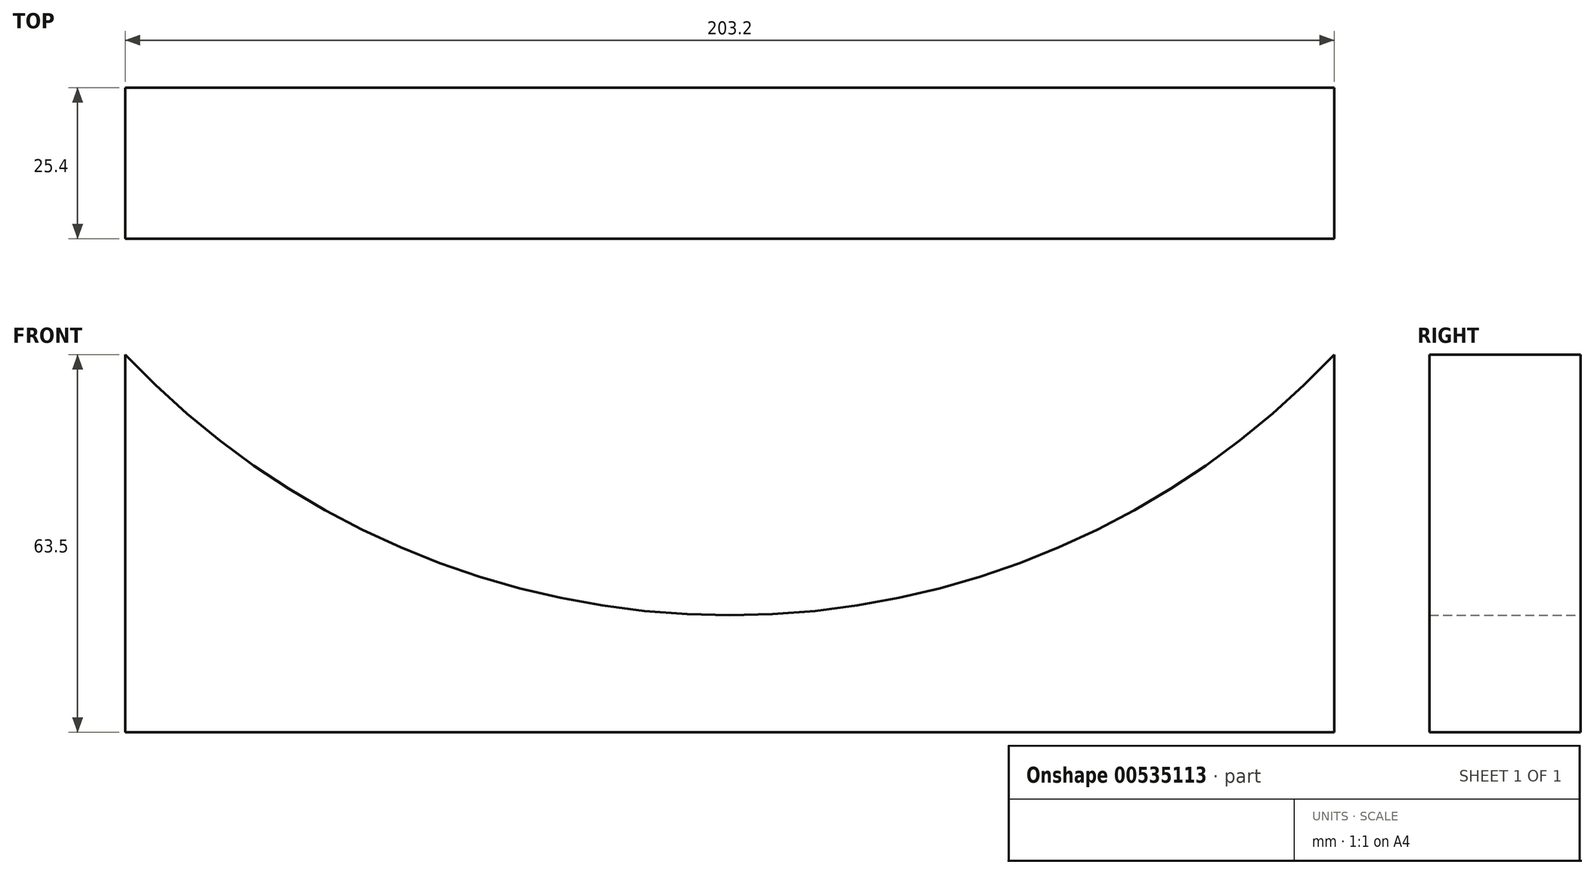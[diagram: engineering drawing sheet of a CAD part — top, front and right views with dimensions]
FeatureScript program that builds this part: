
annotation { "Feature Type Name" : "Feature", "Feature Type Description" : "" }
export const myFeature = defineFeature(function(context is Context, id is Id, definition is map)
    precondition{}
    {
        {
            var Q0;
            Q0=qCreatedBy(makeId("Front.planeOp"),FACE);
            var sketch = newSketch(context, id + "F0", { "sketchPlane" : qUnion([Q0])});
            skLineSegment(sketch, "E0.bottom", {"start": v(0, 0) * mm, "end": v(203.2, 0) * mm});
            skLineSegment(sketch, "E0.left", {"start": v(0, 0) * mm, "end": v(0, 63.5) * mm});
            skLineSegment(sketch, "E0.right", {"start": v(203.2, 0) * mm, "end": v(203.2, 63.5) * mm});
            skArc(sketch, "E1", {"start": v(0, 63.5) * mm, "mid": v(101.6, 19.68) * mm, "end": v(203.2, 63.5) * mm});
            skSolve(sketch);
        }
        {
            var Q0;
            Q0=makeQuery(id+"F0.imprint","IMPRINT",FACE,{"disambiguationData":[TD([[makeQuery(id+"F0.imprint","IMPRINT",EDGE,{"derivedFrom":sQuery(id+"F0.wireOp",EDGE,"E0.bottom")}),1.0]])]});
            extrude(context, id + "F1", {"entities" : qUnion([Q0]), "depth" : 25.4 * mm});
        }
    });
